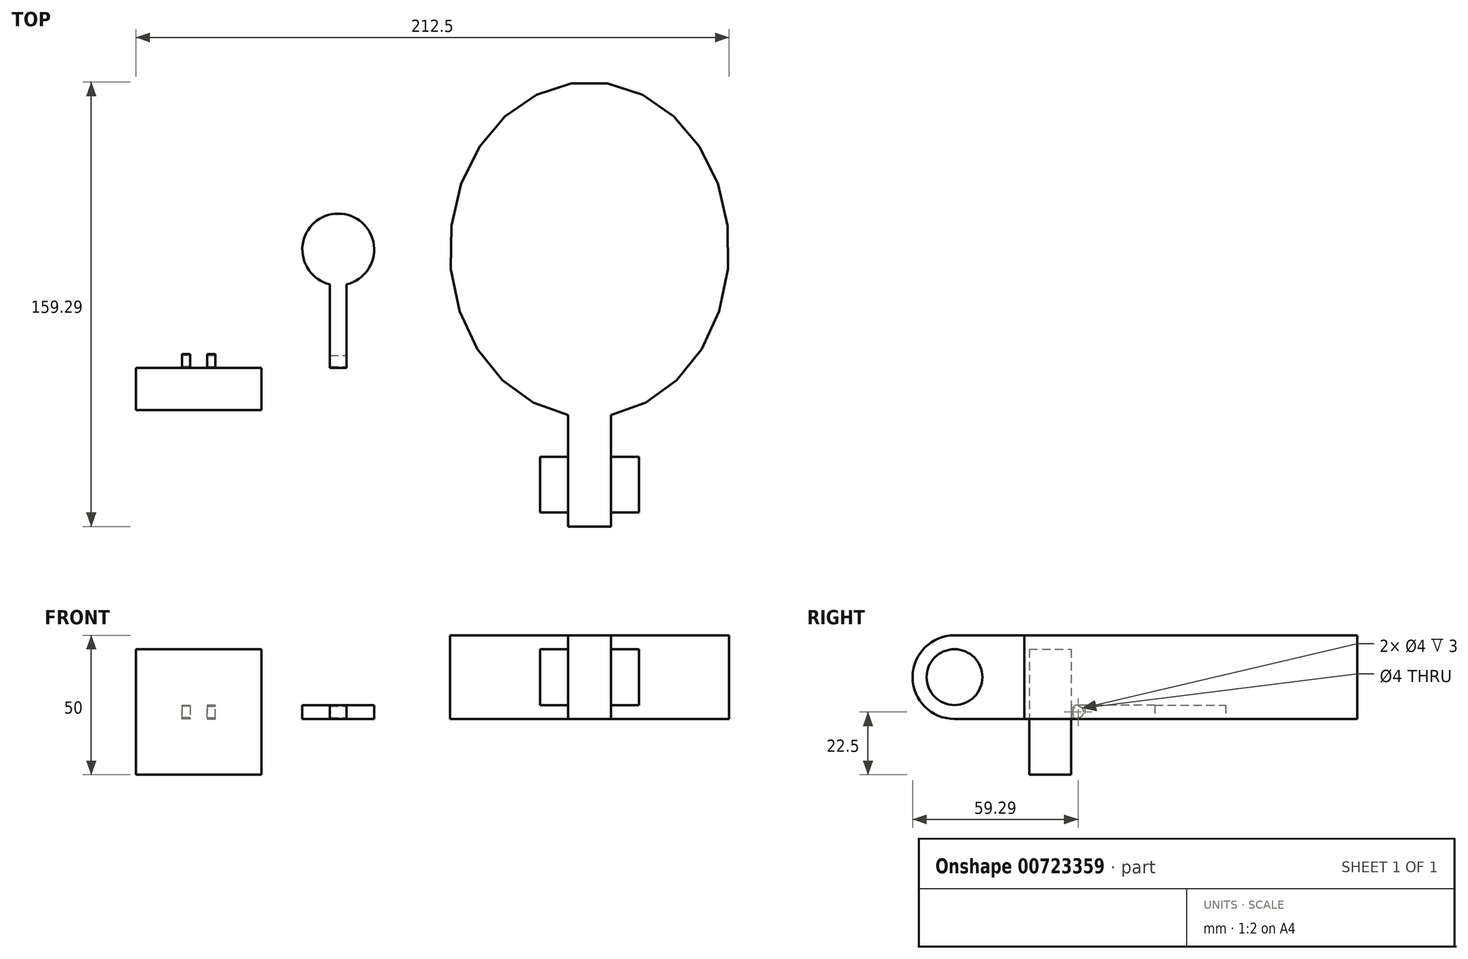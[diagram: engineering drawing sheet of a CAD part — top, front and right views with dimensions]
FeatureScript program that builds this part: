
annotation { "Feature Type Name" : "Feature", "Feature Type Description" : "" }
export const myFeature = defineFeature(function(context is Context, id is Id, definition is map)
    precondition{}
    {
        {
            var Q0;
            Q0=qCreatedBy(makeId("Top.planeOp"),FACE);
            var sketch = newSketch(context, id + "F0", { "sketchPlane" : qUnion([Q0])});
            skCircle(sketch, "E0", {"center": v(0, 0) * mm, "radius": 12.5 * mm});
            skPoint(sketch, "E1", {"position": v(-3, -12.5) * mm});
            skPoint(sketch, "E2", {"position": v(3, -12.5) * mm});
            skLineSegment(sketch, "E3", {"start": v(-3, -12.5) * mm, "end": v(-3, -42.5) * mm});
            skLineSegment(sketch, "E4", {"start": v(3, -12.5) * mm, "end": v(3, -42.5) * mm});
            skLineSegment(sketch, "E5", {"start": v(-3, -42.5) * mm, "end": v(3, -42.5) * mm});
            skLineSegment(sketch, "E6", {"start": v(-3, -12.5) * mm, "end": v(3, -12.5) * mm});
            skCircle(sketch, "E7", {"center": v(0, 0) * mm, "radius": 12.85 * mm});
            skSolve(sketch);
        }
        {
            var Q0;
            Q0=makeQuery(id+"F0.imprint","IMPRINT",FACE,{"disambiguationData":[TD([[makeQuery(id+"F0.imprint","IMPRINT",EDGE,{"derivedFrom":sQuery(id+"F0.wireOp",EDGE,"E0")}),1.0]])]});
            extrude(context, id + "F1", {"entities" : qUnion([Q0]), "depth" : 5 * mm, "offsetDistance" : 25 * mm});
        }
        {
            var Q0;
            Q0 = qSketchRegion(id + "F0", true);
            extrude(context, id + "F2", {"entities" : qUnion([Q0]), "operationType" : NewBodyOperationType.ADD, "depth" : 5 * mm, "offsetDistance" : 25 * mm});
        }
        {
            var Q0;
            Q0=makeQuery(id+"F2.opExtrude","SWEPT_FACE",FACE,{"disambiguationData":[OSD([sQuery(id+"F0.wireOp",EDGE,"E4")])]});
            var sketch = newSketch(context, id + "F3", { "sketchPlane" : qUnion([Q0])});
            skLineSegment(sketch, "E8", {"start": v(-42.5, 2.5) * mm, "end": v(-40, 2.5) * mm});
            skCircle(sketch, "E9", {"center": v(-40, 2.5) * mm, "radius": 2 * mm});
            skPoint(sketch, "E10", {"position": v(-42, 2.5) * mm});
            skLineSegment(sketch, "E11", {"start": v(-40, 2.5) * mm, "end": v(-40, 5) * mm});
            skPoint(sketch, "E12", {"position": v(-40, 4.5) * mm});
            skSolve(sketch);
        }
        {
            var Q0;
            Q0=makeQuery(id+"F3.imprint","IMPRINT",FACE,{"disambiguationData":[TD([[makeQuery(id+"F3.imprint","IMPRINT",EDGE,{"derivedFrom":sQuery(id+"F3.wireOp",EDGE,"E9")}),1.0]])]});
            extrude(context, id + "F4", {"entities" : qUnion([Q0]), "operationType" : NewBodyOperationType.REMOVE, "oppositeDirection" : true, "depth" : 10 * mm, "offsetDistance" : 25 * mm});
        }
        {
            var Q0;
            Q0=qCreatedBy(makeId("Top.planeOp"),FACE);
            var sketch = newSketch(context, id + "F5", { "sketchPlane" : qUnion([Q0])});
            skLineSegment(sketch, "E13", {"start": v(0, 0) * mm, "end": v(-50, 0) * mm});
            skLineSegment(sketch, "E14", {"start": v(-50, 0) * mm, "end": v(-50, -50) * mm});
            skLineSegment(sketch, "E15.bottom", {"start": v(-27.5, -57.5) * mm, "end": v(-72.5, -57.5) * mm});
            skLineSegment(sketch, "E15.top", {"start": v(-27.5, -42.5) * mm, "end": v(-72.5, -42.5) * mm});
            skLineSegment(sketch, "E15.left", {"start": v(-27.5, -57.5) * mm, "end": v(-27.5, -42.5) * mm});
            skLineSegment(sketch, "E15.right", {"start": v(-72.5, -57.5) * mm, "end": v(-72.5, -42.5) * mm});
            skPoint(sketch, "E15.middle", {"position": v(-50, -50) * mm});
            skPoint(sketch, "E16", {"position": v(-53.25, -42.5) * mm});
            skPoint(sketch, "E17", {"position": v(-46.75, -42.5) * mm});
            skLineSegment(sketch, "E18.bottom", {"start": v(-53.25, -42.5) * mm, "end": v(-46.75, -42.5) * mm});
            skLineSegment(sketch, "E18.top", {"start": v(-53.25, -47.5) * mm, "end": v(-46.75, -47.5) * mm});
            skLineSegment(sketch, "E18.left", {"start": v(-53.25, -42.5) * mm, "end": v(-53.25, -47.5) * mm});
            skLineSegment(sketch, "E18.right", {"start": v(-46.75, -42.5) * mm, "end": v(-46.75, -47.5) * mm});
            skSolve(sketch);
        }
        {
            var Q0;
            Q0=makeQuery(id+"F5.imprint","IMPRINT",FACE,{"disambiguationData":[TD([[makeQuery(id+"F5.imprint","IMPRINT",EDGE,{"derivedFrom":sQuery(id+"F5.wireOp",EDGE,"E15.bottom")}),-1.0]])]});
            extrude(context, id + "F6", {"entities" : qUnion([Q0]), "depth" : 5 * mm, "offsetDistance" : 25 * mm});
        }
        {
            var Q0;
            Q0=makeQuery(id+"F6.opExtrude","CAP_FACE",FACE,{"disambiguationData":[OSD([sQuery(id+"F5.wireOp",EDGE,"E15.bottom"),sQuery(id+"F5.wireOp",EDGE,"E15.top"),sQuery(id+"F5.wireOp",EDGE,"E15.left"),sQuery(id+"F5.wireOp",EDGE,"E15.right"),sQuery(id+"F5.wireOp",EDGE,"E18.top"),sQuery(id+"F5.wireOp",EDGE,"E18.left"),sQuery(id+"F5.wireOp",EDGE,"E18.right")])],"isStart":false});
            var sketch = newSketch(context, id + "F7", { "sketchPlane" : qUnion([Q0])});
            skLineSegment(sketch, "E19.bottom", {"start": v(-72.5, -42.5) * mm, "end": v(-27.5, -42.5) * mm});
            skLineSegment(sketch, "E19.top", {"start": v(-72.5, -57.5) * mm, "end": v(-27.5, -57.5) * mm});
            skLineSegment(sketch, "E19.left", {"start": v(-72.5, -42.5) * mm, "end": v(-72.5, -57.5) * mm});
            skLineSegment(sketch, "E19.right", {"start": v(-27.5, -42.5) * mm, "end": v(-27.5, -57.5) * mm});
            skSolve(sketch);
        }
        {
            var Q0;
            Q0=makeQuery(id+"F7.imprint","IMPRINT",FACE,{"disambiguationData":[TD([[makeQuery(id+"F7.imprint","IMPRINT",EDGE,{"derivedFrom":sQuery(id+"F7.wireOp",EDGE,"E19.top")}),-1.0]])]});
            extrude(context, id + "F8", {"entities" : qUnion([Q0]), "operationType" : NewBodyOperationType.ADD, "depth" : 20 * mm, "offsetDistance" : 25 * mm});
        }
        {
            var Q0;
            Q0=makeQuery(id+"F6.opExtrude","CAP_FACE",FACE,{"disambiguationData":[OSD([sQuery(id+"F5.wireOp",EDGE,"E15.bottom"),sQuery(id+"F5.wireOp",EDGE,"E15.top"),sQuery(id+"F5.wireOp",EDGE,"E15.left"),sQuery(id+"F5.wireOp",EDGE,"E15.right"),sQuery(id+"F5.wireOp",EDGE,"E18.top"),sQuery(id+"F5.wireOp",EDGE,"E18.left"),sQuery(id+"F5.wireOp",EDGE,"E18.right")])],"isStart":true});
            var sketch = newSketch(context, id + "F9", { "sketchPlane" : qUnion([Q0])});
            skLineSegment(sketch, "E20.bottom", {"start": v(-27.5, 42.5) * mm, "end": v(-72.5, 42.5) * mm});
            skLineSegment(sketch, "E20.top", {"start": v(-27.5, 57.5) * mm, "end": v(-72.5, 57.5) * mm});
            skLineSegment(sketch, "E20.left", {"start": v(-27.5, 42.5) * mm, "end": v(-27.5, 57.5) * mm});
            skLineSegment(sketch, "E20.right", {"start": v(-72.5, 42.5) * mm, "end": v(-72.5, 57.5) * mm});
            skSolve(sketch);
        }
        {
            var Q0;
            Q0=makeQuery(id+"F9.imprint","IMPRINT",FACE,{"disambiguationData":[TD([[makeQuery(id+"F9.imprint","IMPRINT",EDGE,{"derivedFrom":sQuery(id+"F9.wireOp",EDGE,"E20.top")}),1.0]])]});
            extrude(context, id + "F10", {"entities" : qUnion([Q0]), "operationType" : NewBodyOperationType.ADD, "depth" : 20 * mm, "offsetDistance" : 25 * mm});
        }
        {
            var Q0;
            Q0=makeQuery(id+"F2.opExtrude","CAP_EDGE",EDGE,{"disambiguationData":[OSD([sQuery(id+"F0.wireOp",EDGE,"E5")])],"isStart":false});
            fillet(context, id + "F11", {"entities" : qUnion([Q0]), "radius" : 2.5 * mm, "tangentPropagation" : true, "allowEdgeOverflow" : false});
        }
        {
            var Q0;
            Q0=makeQuery(id+"F2.opExtrude","CAP_EDGE",EDGE,{"disambiguationData":[OSD([sQuery(id+"F0.wireOp",EDGE,"E5")])],"isStart":true});
            fillet(context, id + "F12", {"entities" : qUnion([Q0]), "radius" : 2.5 * mm, "tangentPropagation" : true, "allowEdgeOverflow" : false});
        }
        {
            var Q0;
            {var subQ0=sQuery(id+"F5.wireOp",EDGE,"E18.top");Q0=makeQuery(id+"F10.boolean.opBoolean","MERGE",FACE,{"derivedFrom":[makeQuery(id+"F8.boolean.opBoolean","MERGE",FACE,{"derivedFrom":[makeQuery(id+"F6.opExtrude","SWEPT_FACE",FACE,{"disambiguationData":[OSD([subQ0])]}),makeQuery(id+"F8.opExtrude","SWEPT_FACE",FACE,{"disambiguationData":[OSD([subQ0])]})]}),makeQuery(id+"F10.opExtrude","SWEPT_FACE",FACE,{"disambiguationData":[OSD([subQ0])]})]});}
            var sketch = newSketch(context, id + "F13", { "sketchPlane" : qUnion([Q0])});
            skSolve(sketch);
        }
        {
            var Q0;
            Q0 = qSketchRegion(id + "F13", true);
            var Q1;
            {var subQ0=sQuery(id+"F5.wireOp",EDGE,"E18.top");Q1=makeQuery(id+"F13.imprint","IMPRINT",FACE,{"disambiguationData":[TD([[makeQuery(id+"F13.imprint","IMPRINT",EDGE,{"derivedFrom":makeQuery(id+"F8.opExtrude","CAP_EDGE",EDGE,{"disambiguationData":[OSD([subQ0])],"isStart":false})}),1.0]])]});}
            extrude(context, id + "F14", {"entities" : qUnion([Q0, Q1]), "operationType" : NewBodyOperationType.ADD, "depth" : 5 * mm, "offsetDistance" : 25 * mm});
        }
        {
            var Q0;
            {var subQ0=sQuery(id+"F5.wireOp",EDGE,"E18.right");var subQ1=sQuery(id+"F5.wireOp",EDGE,"E18.left");var subQ2=sQuery(id+"F9.wireOp",EDGE,"E20.bottom");var subQ3=sQuery(id+"F7.wireOp",EDGE,"E19.bottom");var subQ4=sQuery(id+"F5.wireOp",EDGE,"E15.top");Q0=makeQuery(id+"F14.boolean.opBoolean","MERGE",FACE,{"derivedFrom":[makeQuery(id+"F10.boolean.opBoolean","MERGE",FACE,{"derivedFrom":[makeQuery(id+"F8.boolean.opBoolean","MERGE",FACE,{"derivedFrom":[makeQuery(id+"F6.opExtrude","SWEPT_FACE",FACE,{"disambiguationData":[OSD([subQ4]),TDD([makeQuery(id+"F5.imprint","IMPRINT",EDGE,{"disambiguationData":[TD([[makeQuery(id+"F5.imprint","INTERSECT",VERTEX,{"derivedFrom":[subQ4,sQuery(id+"F5.wireOp",EDGE,"E15.left")]}),-1.0]])],"derivedFrom":subQ4})])]}),makeQuery(id+"F8.opExtrude","SWEPT_FACE",FACE,{"disambiguationData":[OSD([subQ3]),TDD([makeQuery(id+"F7.imprint","IMPRINT",EDGE,{"disambiguationData":[TD([[makeQuery(id+"F7.imprint","INTERSECT",VERTEX,{"derivedFrom":[subQ3,sQuery(id+"F7.wireOp",EDGE,"E19.right")]}),-1.0],[makeQuery(id+"F7.imprint","INTERSECT",VERTEX,{"derivedFrom":[makeQuery(id+"F6.opExtrude","CAP_EDGE",EDGE,{"disambiguationData":[OSD([subQ0])],"isStart":false}),subQ3]}),1.0]])],"derivedFrom":subQ3})])]})]}),makeQuery(id+"F10.opExtrude","SWEPT_FACE",FACE,{"disambiguationData":[OSD([subQ2]),TDD([makeQuery(id+"F9.imprint","IMPRINT",EDGE,{"disambiguationData":[TD([[makeQuery(id+"F9.imprint","INTERSECT",VERTEX,{"derivedFrom":[subQ2,sQuery(id+"F9.wireOp",EDGE,"E20.left")]}),-1.0]])],"derivedFrom":subQ2})])]})]}),makeQuery(id+"F10.boolean.opBoolean","MERGE",FACE,{"derivedFrom":[makeQuery(id+"F8.boolean.opBoolean","MERGE",FACE,{"derivedFrom":[makeQuery(id+"F6.opExtrude","SWEPT_FACE",FACE,{"disambiguationData":[OSD([subQ4]),TDD([makeQuery(id+"F5.imprint","IMPRINT",EDGE,{"disambiguationData":[TD([[makeQuery(id+"F5.imprint","INTERSECT",VERTEX,{"derivedFrom":[subQ4,sQuery(id+"F5.wireOp",EDGE,"E15.right")]}),1.0]])],"derivedFrom":subQ4})])]}),makeQuery(id+"F8.opExtrude","SWEPT_FACE",FACE,{"disambiguationData":[OSD([subQ3]),TDD([makeQuery(id+"F7.imprint","IMPRINT",EDGE,{"disambiguationData":[TD([[makeQuery(id+"F7.imprint","INTERSECT",VERTEX,{"derivedFrom":[subQ3,sQuery(id+"F7.wireOp",EDGE,"E19.left")]}),1.0],[makeQuery(id+"F7.imprint","INTERSECT",VERTEX,{"derivedFrom":[makeQuery(id+"F6.opExtrude","CAP_EDGE",EDGE,{"disambiguationData":[OSD([subQ1])],"isStart":false}),subQ3]}),-1.0]])],"derivedFrom":subQ3})])]})]}),makeQuery(id+"F10.opExtrude","SWEPT_FACE",FACE,{"disambiguationData":[OSD([subQ2]),TDD([makeQuery(id+"F9.imprint","IMPRINT",EDGE,{"disambiguationData":[TD([[makeQuery(id+"F9.imprint","INTERSECT",VERTEX,{"derivedFrom":[subQ2,sQuery(id+"F9.wireOp",EDGE,"E20.right")]}),1.0]])],"derivedFrom":subQ2})])]})]}),makeQuery(id+"F14.opExtrude","CAP_FACE",FACE,{"disambiguationData":[OSD([sQuery(id+"F5.wireOp",EDGE,"E18.top"),subQ1,subQ0])],"isStart":false})]});}
            var sketch = newSketch(context, id + "F15", { "sketchPlane" : qUnion([Q0])});
            skPoint(sketch, "E21", {"position": v(50, 2.5) * mm});
            skLineSegment(sketch, "E22.bottom", {"start": v(47, 5) * mm, "end": v(53, 5) * mm});
            skLineSegment(sketch, "E22.top", {"start": v(47, 0) * mm, "end": v(53, 0) * mm});
            skLineSegment(sketch, "E22.left", {"start": v(47, 5) * mm, "end": v(47, 0) * mm});
            skLineSegment(sketch, "E22.right", {"start": v(53, 5) * mm, "end": v(53, 0) * mm});
            skLineSegment(sketch, "E23", {"start": v(53, 0) * mm, "end": v(56, 0) * mm});
            skLineSegment(sketch, "E24", {"start": v(56, 0) * mm, "end": v(56, 5) * mm});
            skLineSegment(sketch, "E25", {"start": v(56, 5) * mm, "end": v(53, 5) * mm});
            skLineSegment(sketch, "E26", {"start": v(47, 0) * mm, "end": v(44, 0) * mm});
            skLineSegment(sketch, "E27", {"start": v(44, 0) * mm, "end": v(44, 5) * mm});
            skLineSegment(sketch, "E28", {"start": v(44, 5) * mm, "end": v(47, 5) * mm});
            skSolve(sketch);
        }
        {
            var Q0;
            Q0=makeQuery(id+"F15.imprint","IMPRINT",FACE,{"disambiguationData":[TD([[makeQuery(id+"F15.imprint","IMPRINT",EDGE,{"derivedFrom":sQuery(id+"F15.wireOp",EDGE,"E22.right")}),1.0]])]});
            var Q1;
            Q1=makeQuery(id+"F15.imprint","IMPRINT",FACE,{"disambiguationData":[TD([[makeQuery(id+"F15.imprint","IMPRINT",EDGE,{"derivedFrom":sQuery(id+"F15.wireOp",EDGE,"E22.left")}),-1.0]])]});
            extrude(context, id + "F16", {"entities" : qUnion([Q0, Q1]), "operationType" : NewBodyOperationType.ADD, "depth" : 5 * mm, "offsetDistance" : 25 * mm});
        }
        {
            var Q0;
            Q0=makeQuery(id+"F16.opExtrude","SWEPT_FACE",FACE,{"disambiguationData":[OSD([sQuery(id+"F15.wireOp",EDGE,"E24")])]});
            var sketch = newSketch(context, id + "F17", { "sketchPlane" : qUnion([Q0])});
            skPoint(sketch, "E29", {"position": v(40, 2.5) * mm});
            skCircle(sketch, "E30", {"center": v(40, 2.5) * mm, "radius": 2 * mm});
            skSolve(sketch);
        }
        {
            var Q0;
            Q0=makeQuery(id+"F17.imprint","IMPRINT",FACE,{"disambiguationData":[TD([[makeQuery(id+"F17.imprint","IMPRINT",EDGE,{"derivedFrom":sQuery(id+"F17.wireOp",EDGE,"E30")}),1.0]])]});
            extrude(context, id + "F18", {"entities" : qUnion([Q0]), "operationType" : NewBodyOperationType.REMOVE, "oppositeDirection" : true, "depth" : 3 * mm, "offsetDistance" : 25 * mm});
        }
        {
            var Q0;
            Q0=makeQuery(id+"F16.opExtrude","SWEPT_FACE",FACE,{"disambiguationData":[OSD([sQuery(id+"F15.wireOp",EDGE,"E27")])]});
            var sketch = newSketch(context, id + "F19", { "sketchPlane" : qUnion([Q0])});
            skPoint(sketch, "E31", {"position": v(-40, 2.5) * mm});
            skCircle(sketch, "E32", {"center": v(-40, 2.5) * mm, "radius": 2 * mm});
            skSolve(sketch);
        }
        {
            var Q0;
            Q0=makeQuery(id+"F19.imprint","IMPRINT",FACE,{"disambiguationData":[TD([[makeQuery(id+"F19.imprint","IMPRINT",EDGE,{"derivedFrom":sQuery(id+"F19.wireOp",EDGE,"E32")}),1.0]])]});
            extrude(context, id + "F20", {"entities" : qUnion([Q0]), "operationType" : NewBodyOperationType.REMOVE, "oppositeDirection" : true, "depth" : 3 * mm, "offsetDistance" : 25 * mm});
        }
        {
            var Q0;
            Q0=qCreatedBy(makeId("Top.planeOp"),FACE);
            var sketch = newSketch(context, id + "F21", { "sketchPlane" : qUnion([Q0])});
            skLineSegment(sketch, "E33", {"start": v(0, 0) * mm, "end": v(90, 0) * mm});
            skEllipse(sketch, "E34", {"center": v(90, 0) * mm, "majorRadius": 60 * mm, "minorRadius": 50 * mm, "majorAxis": v(0, -1)});
            skLineSegment(sketch, "E35", {"start": v(90, 0) * mm, "end": v(90, -60) * mm});
            skPoint(sketch, "E36", {"position": v(82.31, -59.29) * mm});
            skPoint(sketch, "E37", {"position": v(97.69, -59.29) * mm});
            skLineSegment(sketch, "E38.bottom", {"start": v(82.31, -59.29) * mm, "end": v(97.69, -59.29) * mm});
            skLineSegment(sketch, "E38.top", {"start": v(82.31, -99.29) * mm, "end": v(97.69, -99.29) * mm});
            skLineSegment(sketch, "E38.left", {"start": v(82.31, -59.29) * mm, "end": v(82.31, -99.29) * mm});
            skLineSegment(sketch, "E38.right", {"start": v(97.69, -59.29) * mm, "end": v(97.69, -99.29) * mm});
            skSolve(sketch);
        }
        {
            var Q0;
            Q0=makeQuery(id+"F21.imprint","IMPRINT",FACE,{"disambiguationData":[TD([[makeQuery(id+"F21.imprint","IMPRINT",EDGE,{"derivedFrom":sQuery(id+"F21.wireOp",EDGE,"E34")}),1.0]])]});
            extrude(context, id + "F22", {"entities" : qUnion([Q0]), "depth" : 30 * mm, "offsetDistance" : 25 * mm});
        }
        {
            var Q0;
            Q0 = qSketchRegion(id + "F21", true);
            extrude(context, id + "F23", {"entities" : qUnion([Q0]), "operationType" : NewBodyOperationType.ADD, "depth" : 30 * mm, "offsetDistance" : 25 * mm});
        }
        {
            var Q0;
            Q0=makeQuery(id+"F23.opExtrude","SWEPT_FACE",FACE,{"disambiguationData":[OSD([sQuery(id+"F21.wireOp",EDGE,"E38.right")])]});
            var sketch = newSketch(context, id + "F24", { "sketchPlane" : qUnion([Q0])});
            skPoint(sketch, "E39", {"position": v(-84.29, 15) * mm});
            skCircle(sketch, "E40", {"center": v(-84.29, 15) * mm, "radius": 10 * mm});
            skPoint(sketch, "E41", {"position": v(-74.29, 15) * mm});
            skPoint(sketch, "E42", {"position": v(-99.29, 15) * mm});
            skLineSegment(sketch, "E43", {"start": v(-99.29, 15) * mm, "end": v(-84.29, 15) * mm});
            skSolve(sketch);
        }
        {
            var Q0;
            Q0=makeQuery(id+"F24.imprint","IMPRINT",FACE,{"disambiguationData":[TD([[makeQuery(id+"F24.imprint","IMPRINT",EDGE,{"derivedFrom":sQuery(id+"F24.wireOp",EDGE,"E40")}),1.0]])]});
            extrude(context, id + "F25", {"entities" : qUnion([Q0]), "operationType" : NewBodyOperationType.ADD, "depth" : 10 * mm, "offsetDistance" : 25 * mm});
        }
        {
            var Q0;
            Q0=makeQuery(id+"F23.opExtrude","SWEPT_FACE",FACE,{"disambiguationData":[OSD([sQuery(id+"F21.wireOp",EDGE,"E38.left")])]});
            var sketch = newSketch(context, id + "F26", { "sketchPlane" : qUnion([Q0])});
            skCircle(sketch, "E44", {"center": v(84.29, 15) * mm, "radius": 10 * mm});
            skPoint(sketch, "E45", {"position": v(99.29, 15) * mm});
            skLineSegment(sketch, "E46", {"start": v(99.29, 15) * mm, "end": v(84.29, 15) * mm});
            skSolve(sketch);
        }
        {
            var Q0;
            Q0 = qSketchRegion(id + "F26", true);
            extrude(context, id + "F27", {"entities" : qUnion([Q0]), "operationType" : NewBodyOperationType.ADD, "depth" : 10 * mm, "offsetDistance" : 25 * mm});
        }
        {
            var Q0;
            Q0=makeQuery(id+"F23.opExtrude","CAP_EDGE",EDGE,{"disambiguationData":[OSD([sQuery(id+"F21.wireOp",EDGE,"E38.top")])],"isStart":false});
            fillet(context, id + "F28", {"entities" : qUnion([Q0]), "radius" : 15 * mm, "tangentPropagation" : true, "allowEdgeOverflow" : false});
        }
        {
            var Q0;
            Q0=makeQuery(id+"F23.opExtrude","CAP_EDGE",EDGE,{"disambiguationData":[OSD([sQuery(id+"F21.wireOp",EDGE,"E38.top")])],"isStart":true});
            fillet(context, id + "F29", {"entities" : qUnion([Q0]), "radius" : 15 * mm, "tangentPropagation" : true, "allowEdgeOverflow" : false});
        }
    });
